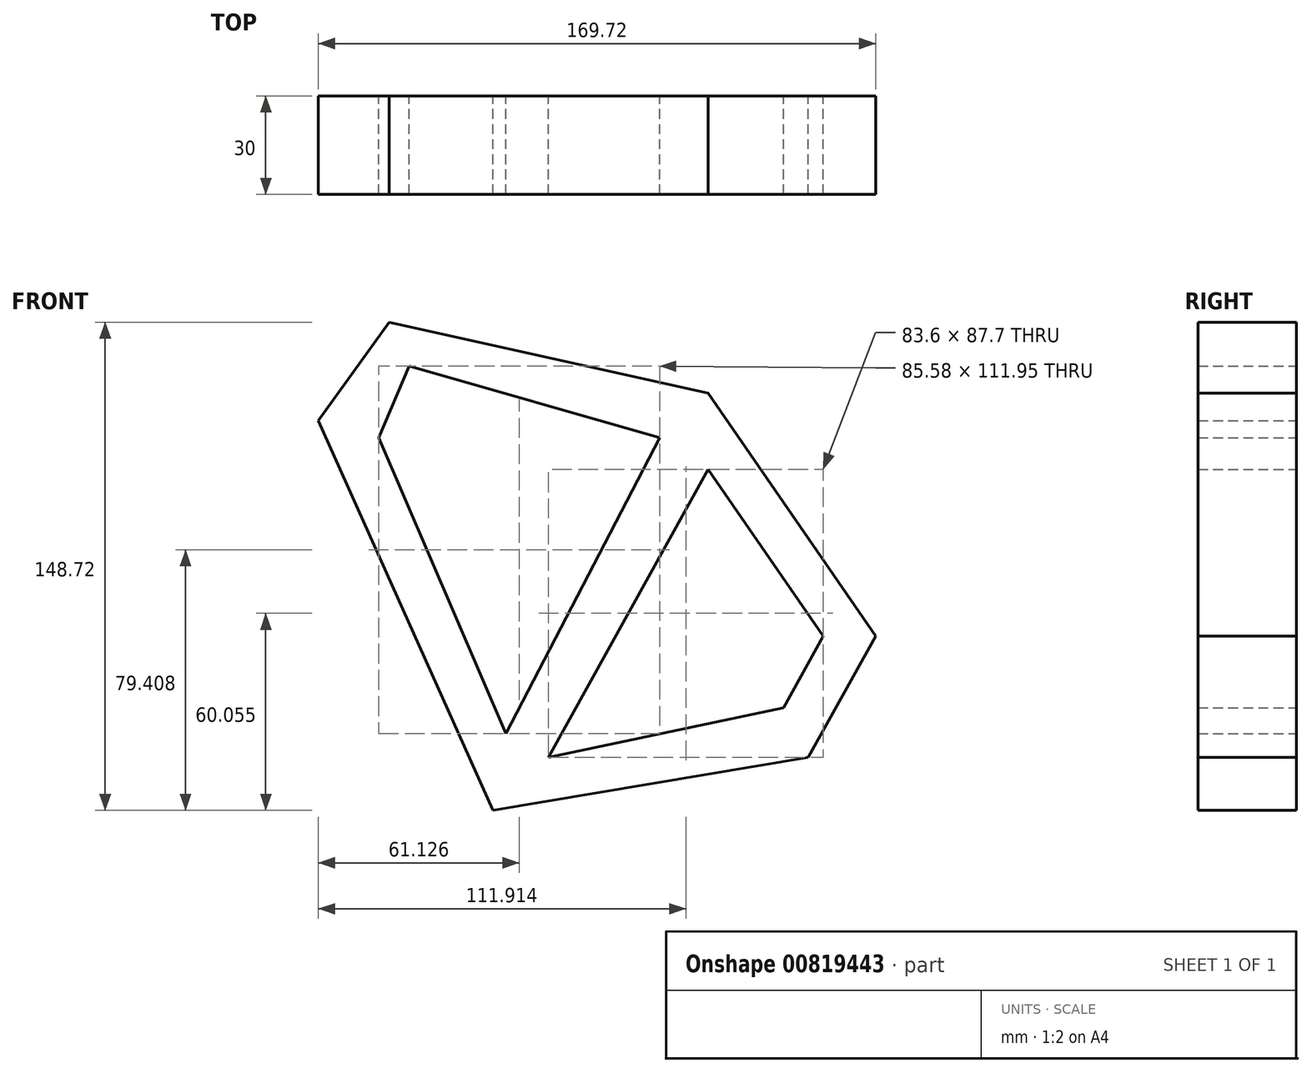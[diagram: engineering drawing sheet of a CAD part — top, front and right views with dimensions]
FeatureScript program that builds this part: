
annotation { "Feature Type Name" : "Feature", "Feature Type Description" : "" }
export const myFeature = defineFeature(function(context is Context, id is Id, definition is map)
    precondition{}
    {
        {
            var Q0;
            Q0=qCreatedBy(makeId("Front.planeOp"),FACE);
            var sketch = newSketch(context, id + "F0", { "sketchPlane" : qUnion([Q0])});
            skLineSegment(sketch, "E0", {"start": v(-44.32, 78.63) * mm, "end": v(52.77, 57.03) * mm});
            skLineSegment(sketch, "E1", {"start": v(52.77, 57.03) * mm, "end": v(103.83, -17.04) * mm});
            skLineSegment(sketch, "E2", {"start": v(103.83, -17.04) * mm, "end": v(83.33, -53.88) * mm});
            skLineSegment(sketch, "E3", {"start": v(83.33, -53.88) * mm, "end": v(-12.68, -70.1) * mm});
            skLineSegment(sketch, "E4", {"start": v(-12.68, -70.1) * mm, "end": v(-65.9, 48.67) * mm});
            skLineSegment(sketch, "E5", {"start": v(-65.9, 48.67) * mm, "end": v(-44.32, 78.63) * mm});
            skLineSegment(sketch, "E6", {"start": v(-38.2, 65.3) * mm, "end": v(38.03, 43.43) * mm});
            skLineSegment(sketch, "E7", {"start": v(38.03, 43.43) * mm, "end": v(-8.72, -46.66) * mm});
            skLineSegment(sketch, "E8", {"start": v(-8.72, -46.66) * mm, "end": v(-47.55, 43.43) * mm});
            skLineSegment(sketch, "E9", {"start": v(-47.55, 43.43) * mm, "end": v(-38.2, 65.3) * mm});
            skLineSegment(sketch, "E10", {"start": v(52.77, 33.81) * mm, "end": v(87.82, -17.04) * mm});
            skLineSegment(sketch, "E11", {"start": v(87.82, -17.04) * mm, "end": v(75.78, -38.8) * mm});
            skLineSegment(sketch, "E12", {"start": v(75.78, -38.8) * mm, "end": v(4.23, -53.88) * mm});
            skLineSegment(sketch, "E13", {"start": v(4.23, -53.88) * mm, "end": v(52.77, 33.81) * mm});
            skSolve(sketch);
        }
        {
            var Q0;
            Q0 = qSketchRegion(id + "F0", true);
            extrude(context, id + "F1", {"entities" : qUnion([Q0]), "depth" : 30 * mm, "offsetDistance" : 25.4 * mm});
        }
    });
